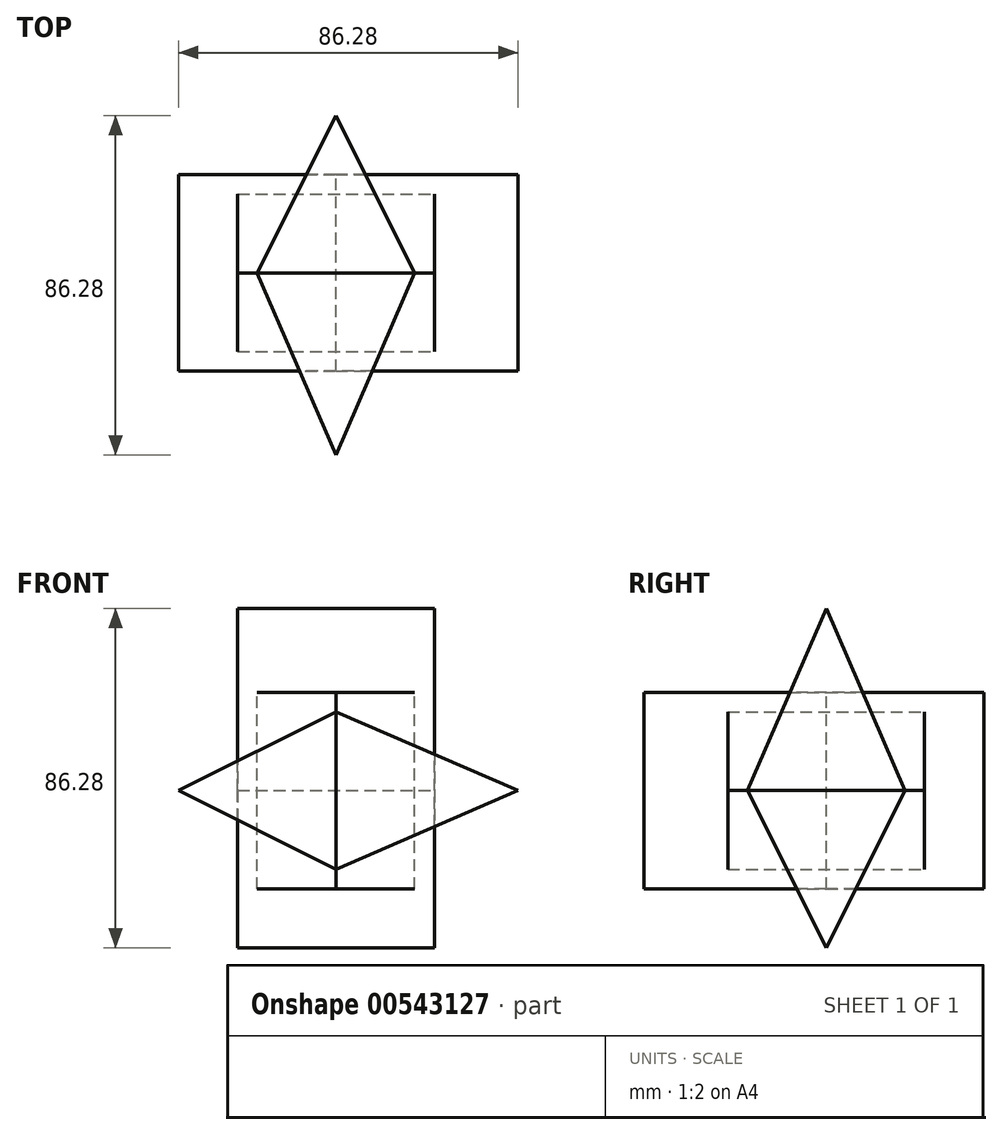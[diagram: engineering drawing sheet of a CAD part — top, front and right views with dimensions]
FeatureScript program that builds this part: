
annotation { "Feature Type Name" : "Feature", "Feature Type Description" : "" }
export const myFeature = defineFeature(function(context is Context, id is Id, definition is map)
    precondition{}
    {
        {
            var Q0;
            Q0=qCreatedBy(makeId("Front.planeOp"),FACE);
            var sketch = newSketch(context, id + "F0", { "sketchPlane" : qUnion([Q0])});
            skLineSegment(sketch, "E0", {"start": v(46.28, 0) * mm, "end": v(0, 20) * mm});
            skLineSegment(sketch, "E1", {"start": v(0, 20) * mm, "end": v(-40, 0) * mm});
            skLineSegment(sketch, "E2", {"start": v(-40, 0) * mm, "end": v(0, -20) * mm});
            skLineSegment(sketch, "E3", {"start": v(0, -20) * mm, "end": v(46.28, 0) * mm});
            skSolve(sketch);
        }
        {
            var Q0;
            Q0=makeQuery(id+"F0.imprint","IMPRINT",FACE,{"disambiguationData":[TD([[makeQuery(id+"F0.imprint","IMPRINT",EDGE,{"derivedFrom":sQuery(id+"F0.wireOp",EDGE,"E0")}),1.0]])]});
            extrude(context, id + "F1", {"entities" : qUnion([Q0]), "depth" : 25 * mm, "offsetDistance" : 25 * mm, "hasSecondDirection" : true, "secondDirectionOppositeDirection" : true, "secondDirectionDepth" : 25 * mm});
        }
        {
            var Q0;
            Q0=qCreatedBy(makeId("Front.planeOp"),FACE);
            var sketch = newSketch(context, id + "F2", { "sketchPlane" : qUnion([Q0])});
            skLineSegment(sketch, "E4", {"start": v(0, 49.78) * mm, "end": v(0, 0) * mm});
            skSolve(sketch);
        }
        {
            var Q0;
            Q0=qCreatedBy(makeId("Front.planeOp"),FACE);
            var sketch = newSketch(context, id + "F3", { "sketchPlane" : qUnion([Q0])});
            skLineSegment(sketch, "E5", {"start": v(60.84, 0) * mm, "end": v(0, 0) * mm});
            skSolve(sketch);
        }
        {
            var Q0;
            Q0=qCreatedBy(makeId("Right.planeOp"),FACE);
            var sketch = newSketch(context, id + "F4", { "sketchPlane" : qUnion([Q0])});
            skLineSegment(sketch, "E6", {"start": v(48.72, 0) * mm, "end": v(-1.84, 0) * mm});
            skSolve(sketch);
        }
        {
            var Q0;
            Q0=makeQuery(id+"F1.opExtrude","SWEPT_BODY",BODY,{"disambiguationData":[OSD([sQuery(id+"F0.wireOp",EDGE,"E0"),sQuery(id+"F0.wireOp",EDGE,"E1"),sQuery(id+"F0.wireOp",EDGE,"E2"),sQuery(id+"F0.wireOp",EDGE,"E3")])]});
            var Q1;
            Q1=sQuery(id+"F2.wireOp",EDGE,"E4");
            transform(context, id + "F5", {"entities" : qUnion([Q0]), "transformType" : TransformType.ROTATION, "transformAxis" : qUnion([Q1]), "angle" : 90 * degree, "makeCopy" : true});
        }
        {
            var Q0;
            Q0=makeQuery(id+"F5.opPattern","COPY",BODY,{"derivedFrom":makeQuery(id+"F1.opExtrude","SWEPT_BODY",BODY,{"disambiguationData":[OSD([sQuery(id+"F0.wireOp",EDGE,"E0"),sQuery(id+"F0.wireOp",EDGE,"E1"),sQuery(id+"F0.wireOp",EDGE,"E2"),sQuery(id+"F0.wireOp",EDGE,"E3")])]}),"instanceName":"1"});
            var Q1;
            Q1=sQuery(id+"F4.wireOp",EDGE,"E6");
            transform(context, id + "F6", {"entities" : qUnion([Q0]), "transformType" : TransformType.ROTATION, "transformAxis" : qUnion([Q1]), "angle" : 90 * degree, "makeCopy" : true});
        }
        {
            var Q0;
            Q0=makeQuery(id+"F5.opPattern","COPY",BODY,{"derivedFrom":makeQuery(id+"F1.opExtrude","SWEPT_BODY",BODY,{"disambiguationData":[OSD([sQuery(id+"F0.wireOp",EDGE,"E0"),sQuery(id+"F0.wireOp",EDGE,"E1"),sQuery(id+"F0.wireOp",EDGE,"E2"),sQuery(id+"F0.wireOp",EDGE,"E3")])]}),"instanceName":"1"});
            var Q1;
            Q1=sQuery(id+"F3.wireOp",EDGE,"E5");
            transform(context, id + "F7", {"entities" : qUnion([Q0]), "transformType" : TransformType.ROTATION, "transformAxis" : qUnion([Q1]), "angle" : 90 * degree, "makeCopy" : false});
        }
    });
